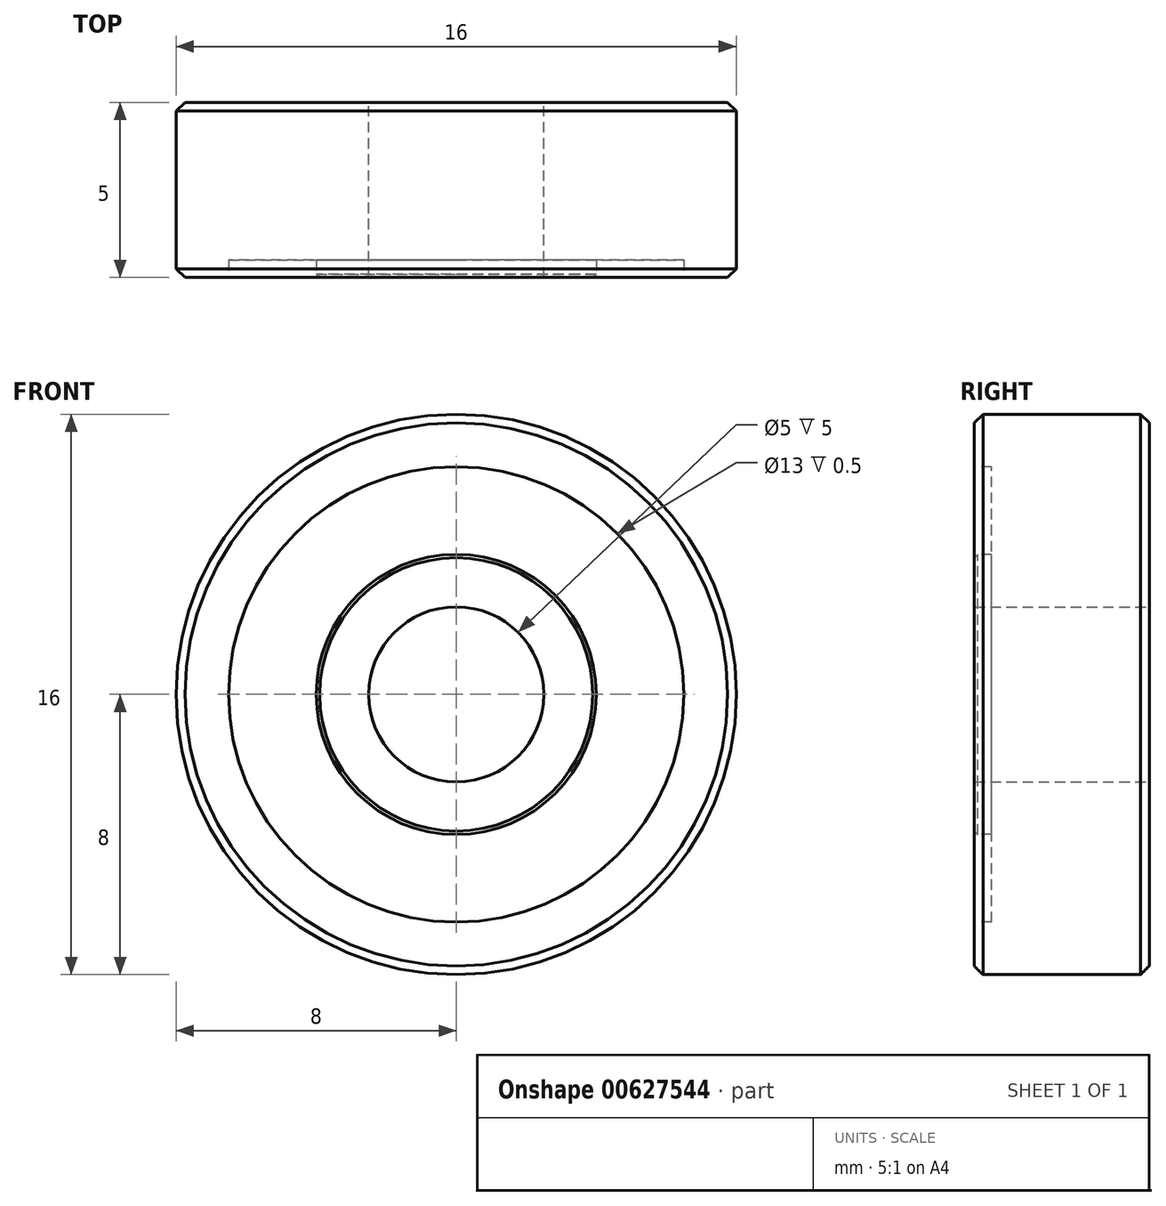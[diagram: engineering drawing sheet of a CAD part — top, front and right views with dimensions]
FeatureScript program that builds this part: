
annotation { "Feature Type Name" : "Feature", "Feature Type Description" : "" }
export const myFeature = defineFeature(function(context is Context, id is Id, definition is map)
    precondition{}
    {
        {
            var Q0;
            Q0=qCreatedBy(makeId("Front.planeOp"),FACE);
            var sketch = newSketch(context, id + "F0", { "sketchPlane" : qUnion([Q0])});
            skCircle(sketch, "E0", {"center": v(0, 0) * mm, "radius": 8 * mm});
            skCircle(sketch, "E1", {"center": v(0, 0) * mm, "radius": 2.5 * mm});
            skSolve(sketch);
        }
        {
            var Q0;
            Q0=makeQuery(id+"F0.imprint","IMPRINT",FACE,{"disambiguationData":[TD([[makeQuery(id+"F0.imprint","IMPRINT",EDGE,{"derivedFrom":sQuery(id+"F0.wireOp",EDGE,"E0")}),1.0]])]});
            extrude(context, id + "F1", {"entities" : qUnion([Q0]), "endBound" : BoundingType.SYMMETRIC, "depth" : 5 * mm, "offsetDistance" : 25 * mm});
        }
        {
            var Q0;
            Q0=makeQuery(id+"F1.opExtrude","CAP_FACE",FACE,{"disambiguationData":[OSD([sQuery(id+"F0.wireOp",EDGE,"E0"),sQuery(id+"F0.wireOp",EDGE,"E1")])],"isStart":false});
            var sketch = newSketch(context, id + "F2", { "sketchPlane" : qUnion([Q0])});
            skCircle(sketch, "E2.0", {"center": v(0, 0) * mm, "radius": 6.5 * mm});
            skCircle(sketch, "E3.0", {"center": v(0, 0) * mm, "radius": 4 * mm});
            skSolve(sketch);
        }
        {
            var Q0;
            Q0 = qSketchRegion(id + "F2", true);
            extrude(context, id + "F3", {"entities" : qUnion([Q0]), "operationType" : NewBodyOperationType.REMOVE, "oppositeDirection" : true, "depth" : 0.5 * mm, "offsetDistance" : 25 * mm});
        }
        {
            var Q0;
            Q0=makeQuery(id+"F1.opExtrude","CAP_EDGE",EDGE,{"disambiguationData":[OSD([sQuery(id+"F0.wireOp",EDGE,"E0")])],"isStart":false});
            var Q1;
            Q1=makeQuery(id+"F1.opExtrude","CAP_EDGE",EDGE,{"disambiguationData":[OSD([sQuery(id+"F0.wireOp",EDGE,"E0")])],"isStart":true});
            chamfer(context, id + "F4", {"entities" : qUnion([Q0, Q1]), "width" : 0.25 * mm, "tangentPropagation" : true});
        }
        {
            var Q0;
            Q0=makeQuery(id+"F3.boolean.opBoolean","COPY",EDGE,{"derivedFrom":makeQuery(id+"F3.opExtrude","CAP_EDGE",EDGE,{"disambiguationData":[OSD([sQuery(id+"F2.wireOp",EDGE,"E2.0")])],"isStart":true})});
            var Q1;
            Q1=makeQuery(id+"F3.boolean.opBoolean","COPY",EDGE,{"derivedFrom":makeQuery(id+"F3.opExtrude","CAP_EDGE",EDGE,{"disambiguationData":[OSD([sQuery(id+"F2.wireOp",EDGE,"E3.0")])],"isStart":true})});
            var Q2;
            Q2=makeQuery(id+"FeYEaoZEhtLTkzV_1.1.F3.boolean.opBoolean","COPY",EDGE,{"derivedFrom":makeQuery(id+"FeYEaoZEhtLTkzV_1.1.F3.opExtrude","CAP_EDGE",EDGE,{"disambiguationData":[OSD([sQuery(id+"F2.wireOp",EDGE,"E2.0")])],"isStart":true})});
            var Q3;
            Q3=makeQuery(id+"FeYEaoZEhtLTkzV_1.1.F3.boolean.opBoolean","COPY",EDGE,{"derivedFrom":makeQuery(id+"FeYEaoZEhtLTkzV_1.1.F3.opExtrude","CAP_EDGE",EDGE,{"disambiguationData":[OSD([sQuery(id+"F2.wireOp",EDGE,"E3.0")])],"isStart":true})});
            chamfer(context, id + "F5", {"entities" : qUnion([Q0, Q1, Q2, Q3]), "width" : 0.1 * mm, "tangentPropagation" : true});
        }
    });
